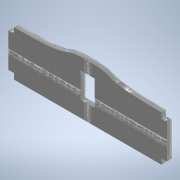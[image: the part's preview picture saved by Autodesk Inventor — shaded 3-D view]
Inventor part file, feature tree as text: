
AUTODESK INVENTOR PART (.ipt)
format: ipt  version: 2020.3 (Build 243373000, 373)  size: 148,480 bytes
history: native  units: mm
features: extrude x3, sketch x3
ambient origin geometry x8: Origin, YZ Plane, XZ Plane, XY Plane, X Axis, Y Axis, Z Axis, Center Point
bodies: Solid1 (feature_tree)
feature tree (6):
  extrude  "Extrusion1"  Depth=10.0mm TaperAngle=0.0deg
  sketch  "Sketch2"  dims[d8=0.0mm d9=0.0mm]
  extrude  "Extrusion2"  [1 undecoded]
  extrude  "Extrusion3"  [1 undecoded]
  sketch  "Sketch1"  dims[d4=4.0mm d5=0.0mm d6=10.0mm d7=0.0mm]
  sketch  "Sketch3"
note: 2 required parameter values undecoded (feature->parameter linkage not recoverable at this tier; creation-order binding heuristic only, values carry confidence <= 0.55)
